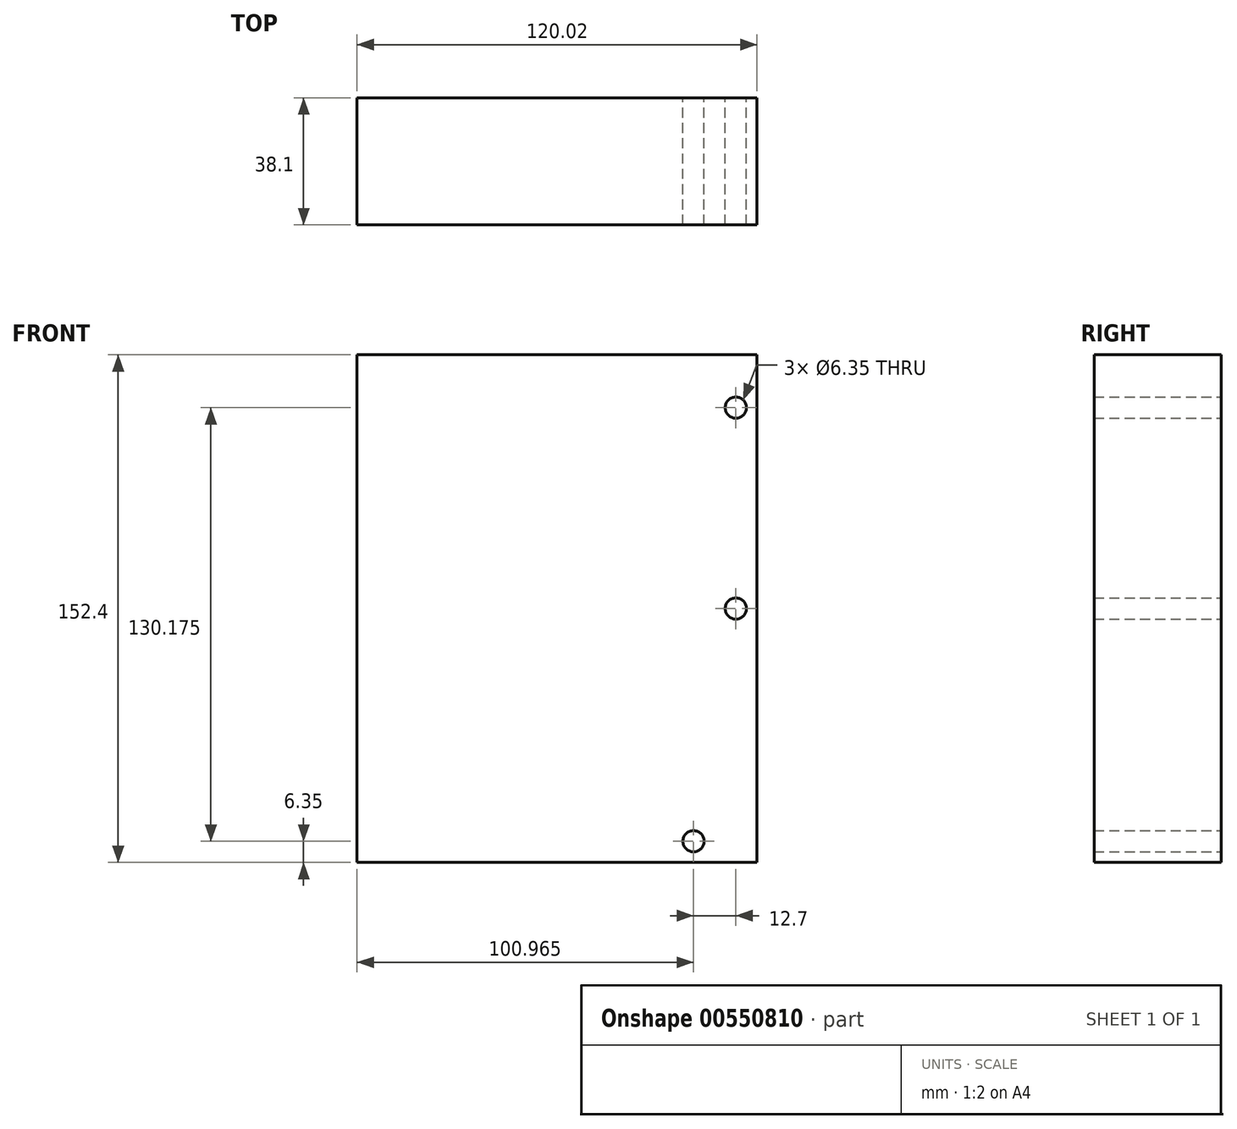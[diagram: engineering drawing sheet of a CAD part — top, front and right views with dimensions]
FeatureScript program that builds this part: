
annotation { "Feature Type Name" : "Feature", "Feature Type Description" : "" }
export const myFeature = defineFeature(function(context is Context, id is Id, definition is map)
    precondition{}
    {
        {
            var Q0;
            Q0=qCreatedBy(makeId("Front.planeOp"),FACE);
            var sketch = newSketch(context, id + "F0", { "sketchPlane" : qUnion([Q0])});
            skLineSegment(sketch, "E0.bottom", {"start": v(0, 0) * mm, "end": v(120.02, 0) * mm});
            skLineSegment(sketch, "E0.top", {"start": v(0, 152.4) * mm, "end": v(120.01, 152.4) * mm});
            skLineSegment(sketch, "E0.left", {"start": v(0, 0) * mm, "end": v(0, 152.4) * mm});
            skLineSegment(sketch, "E0.right", {"start": v(120.02, 0) * mm, "end": v(120.01, 152.4) * mm});
            skLineSegment(sketch, "E1", {"start": v(60, 152.4) * mm, "end": v(60, 0) * mm, "construction": true});
            skLineSegment(sketch, "E2", {"start": v(0, 50.8) * mm, "end": v(120.01, 50.8) * mm, "construction": true});
            skCircle(sketch, "E3", {"center": v(6.35, 136.53) * mm, "radius": 3.18 * mm});
            skCircle(sketch, "E4", {"center": v(6.35, 76.2) * mm, "radius": 3.18 * mm});
            skPoint(sketch, "E4.centerSnap0", {"position": v(0, 76.2) * mm});
            skCircle(sketch, "E5", {"center": v(19.05, 6.35) * mm, "radius": 3.18 * mm});
            skCircle(sketch, "E6.MirrorC", {"center": v(113.66, 76.2) * mm, "radius": 3.18 * mm});
            skCircle(sketch, "E7.MirrorC", {"center": v(113.66, 136.53) * mm, "radius": 3.18 * mm});
            skCircle(sketch, "E8.MirrorC", {"center": v(100.96, 6.35) * mm, "radius": 3.18 * mm});
            skSolve(sketch);
        }
        {
            var Q0;
            Q0=makeQuery(id+"F0.imprint","IMPRINT",FACE,{"disambiguationData":[TD([[makeQuery(id+"F0.imprint","IMPRINT",EDGE,{"derivedFrom":sQuery(id+"F0.wireOp",EDGE,"E4")}),1.0]])]});
            var Q1;
            Q1=makeQuery(id+"F0.imprint","IMPRINT",FACE,{"disambiguationData":[TD([[makeQuery(id+"F0.imprint","IMPRINT",EDGE,{"derivedFrom":sQuery(id+"F0.wireOp",EDGE,"E3")}),1.0]])]});
            var Q2;
            Q2=makeQuery(id+"F0.imprint","IMPRINT",FACE,{"disambiguationData":[TD([[makeQuery(id+"F0.imprint","IMPRINT",EDGE,{"derivedFrom":sQuery(id+"F0.wireOp",EDGE,"E5")}),1.0]])]});
            var Q3;
            Q3=makeQuery(id+"F0.imprint","IMPRINT",FACE,{"disambiguationData":[TD([[makeQuery(id+"F0.imprint","IMPRINT",EDGE,{"derivedFrom":sQuery(id+"F0.wireOp",EDGE,"E8.MirrorC")}),-1.0]])]});
            var Q4;
            Q4=makeQuery(id+"F0.imprint","IMPRINT",FACE,{"disambiguationData":[TD([[makeQuery(id+"F0.imprint","IMPRINT",EDGE,{"derivedFrom":sQuery(id+"F0.wireOp",EDGE,"E6.MirrorC")}),-1.0]])]});
            var Q5;
            Q5=makeQuery(id+"F0.imprint","IMPRINT",FACE,{"disambiguationData":[TD([[makeQuery(id+"F0.imprint","IMPRINT",EDGE,{"derivedFrom":sQuery(id+"F0.wireOp",EDGE,"E7.MirrorC")}),-1.0]])]});
            extrude(context, id + "F1", {"entities" : qUnion([Q0, Q1, Q2, Q3, Q4, Q5]), "depth" : 38.1 * mm, "offsetDistance" : 25.4 * mm});
        }
    });
